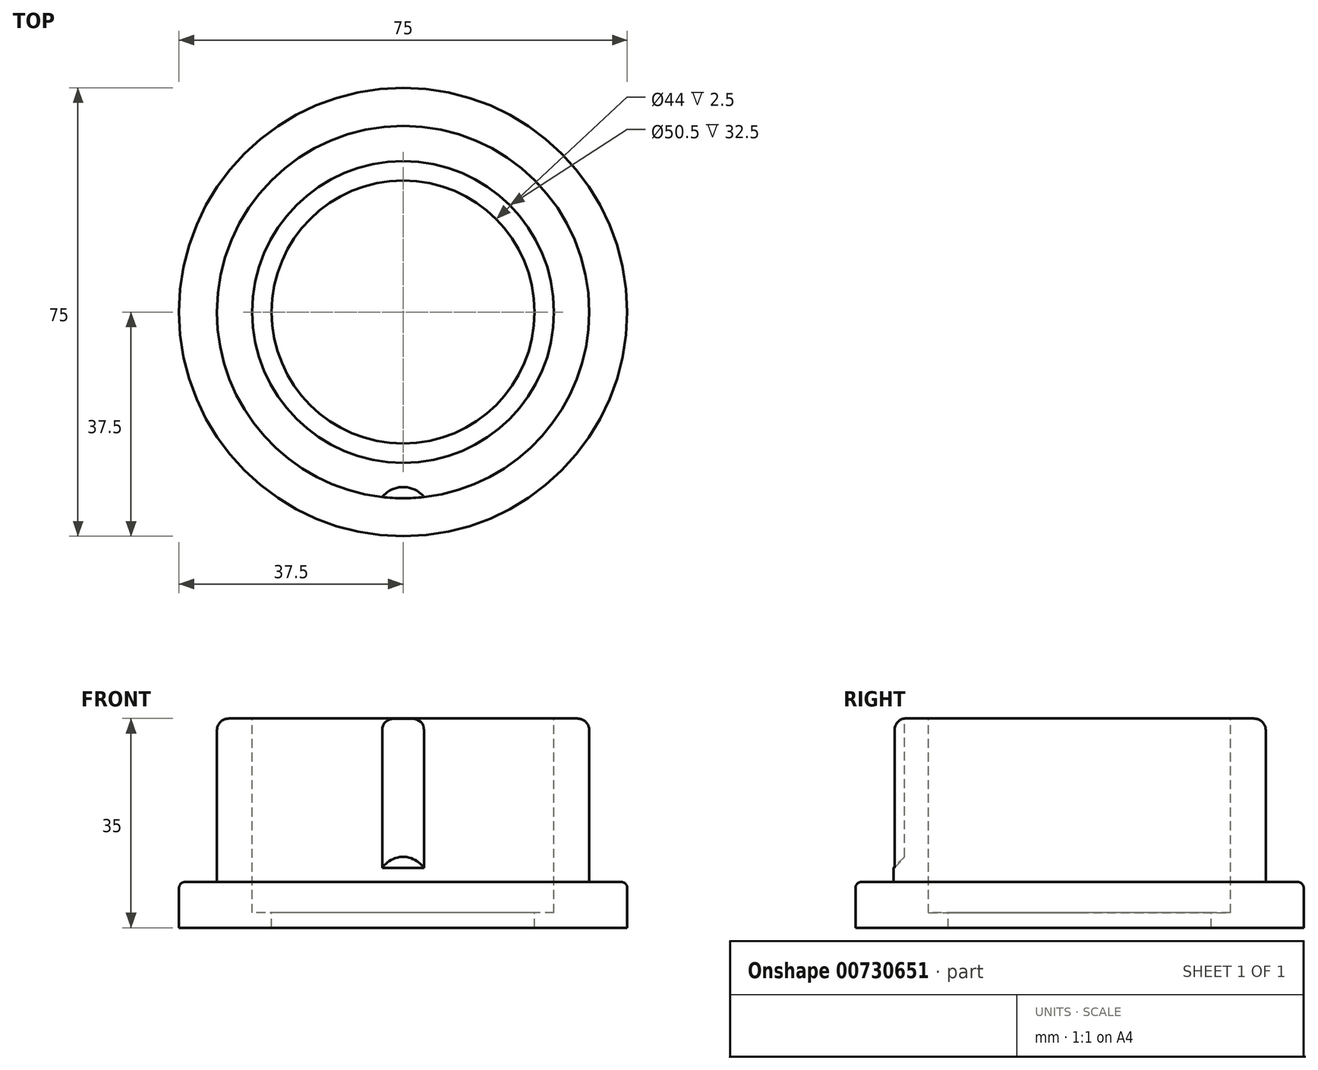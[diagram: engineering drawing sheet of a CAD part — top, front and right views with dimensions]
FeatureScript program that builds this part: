
annotation { "Feature Type Name" : "Feature", "Feature Type Description" : "" }
export const myFeature = defineFeature(function(context is Context, id is Id, definition is map)
    precondition{}
    {
        {
            var Q0;
            Q0=qCreatedBy(makeId("Front.planeOp"),FACE);
            var sketch = newSketch(context, id + "F0", { "sketchPlane" : qUnion([Q0])});
            skLineSegment(sketch, "E0", {"start": v(0, 53.9) * mm, "end": v(0, -40.69) * mm, "construction": true});
            skLineSegment(sketch, "E1", {"start": v(-22, 0) * mm, "end": v(-37.5, 0) * mm});
            skLineSegment(sketch, "E2", {"start": v(-37.5, 0) * mm, "end": v(-37.5, 7.65) * mm});
            skLineSegment(sketch, "E3", {"start": v(-37.5, 7.65) * mm, "end": v(-31.15, 7.65) * mm});
            skLineSegment(sketch, "E4", {"start": v(-31.15, 7.65) * mm, "end": v(-31.15, 35) * mm});
            skLineSegment(sketch, "E5", {"start": v(-25.25, 35) * mm, "end": v(-25.25, 2.5) * mm});
            skLineSegment(sketch, "E6", {"start": v(-31.15, 35) * mm, "end": v(-25.25, 35) * mm});
            skLineSegment(sketch, "E7", {"start": v(-25.25, 2.5) * mm, "end": v(-22, 2.5) * mm});
            skLineSegment(sketch, "E8", {"start": v(-22, 2.5) * mm, "end": v(-22, 0) * mm});
            skSolve(sketch);
        }
        {
            var Q0;
            Q0 = qSketchRegion(id + "F0", true);
            var Q1;
            Q1=sQuery(id+"F0.wireOp",EDGE,"E0");
            revolve(context, id + "F1", {"surfaceOperationType" : NewSurfaceOperationType.NEW, "entities" : qUnion([Q0]), "axis" : qUnion([Q1]), "revolveType" : RevolveType.FULL});
        }
        {
            var Q0;
            Q0=makeQuery(id+"F1.opRevolve","SWEPT_EDGE",EDGE,{"disambiguationData":[OSD([sQuery(id+"F0.wireOp",EDGE,"E2"),sQuery(id+"F0.wireOp",EDGE,"E3")])]});
            fillet(context, id + "F2", {"entities" : qUnion([Q0]), "radius" : 1 * mm, "tangentPropagation" : true, "allowEdgeOverflow" : false});
        }
        {
            var Q0;
            Q0=makeQuery(id+"F1.opRevolve","SWEPT_EDGE",EDGE,{"disambiguationData":[OSD([sQuery(id+"F0.wireOp",EDGE,"E4"),sQuery(id+"F0.wireOp",EDGE,"E6")])]});
            fillet(context, id + "F3", {"entities" : qUnion([Q0]), "radius" : 2 * mm, "tangentPropagation" : true, "allowEdgeOverflow" : false});
        }
        {
            var Q0;
            Q0=makeQuery(id+"F1.opRevolve","SWEPT_FACE",FACE,{"disambiguationData":[OSD([sQuery(id+"F0.wireOp",EDGE,"E6")])]});
            var sketch = newSketch(context, id + "F4", { "sketchPlane" : qUnion([Q0])});
            skArc(sketch, "E9", {"start": v(-3.5, -30.95) * mm, "mid": v(0, -29.28) * mm, "end": v(3.5, -30.95) * mm});
            skArc(sketch, "E10", {"start": v(3.5, -30.95) * mm, "mid": v(0, -31.15) * mm, "end": v(-3.5, -30.95) * mm});
            skCircle(sketch, "E11.0", {"center": v(0, 0) * mm, "radius": 31.15 * mm, "construction": true});
            skSolve(sketch);
        }
        {
            var Q0;
            Q0 = qSketchRegion(id + "F4", true);
            extrude(context, id + "F5", {"entities" : qUnion([Q0]), "operationType" : NewBodyOperationType.REMOVE, "oppositeDirection" : true, "depth" : 23 * mm, "offsetDistance" : 25 * mm});
        }
        {
            var Q0;
            Q0=makeQuery(id+"F5.boolean.opBoolean","INTERSECT",EDGE,{"derivedFrom":[makeQuery(id+"F1.opRevolve","SWEPT_FACE",FACE,{"disambiguationData":[OSD([sQuery(id+"F0.wireOp",EDGE,"E4")])]}),makeQuery(id+"F5.opExtrude","CAP_FACE",FACE,{"disambiguationData":[OSD([sQuery(id+"F4.wireOp",EDGE,"E9"),sQuery(id+"F4.wireOp",EDGE,"E10")])],"isStart":false})]});
            var Q1;
            Q1=makeQuery(id+"F5.boolean.opBoolean","COPY",EDGE,{"derivedFrom":makeQuery(id+"F5.opExtrude","CAP_EDGE",EDGE,{"disambiguationData":[OSD([sQuery(id+"F4.wireOp",EDGE,"E10")])],"isStart":false})});
            chamfer(context, id + "F6", {"entities" : qUnion([Q0, Q1]), "width" : 2 * mm, "tangentPropagation" : true});
        }
    });
